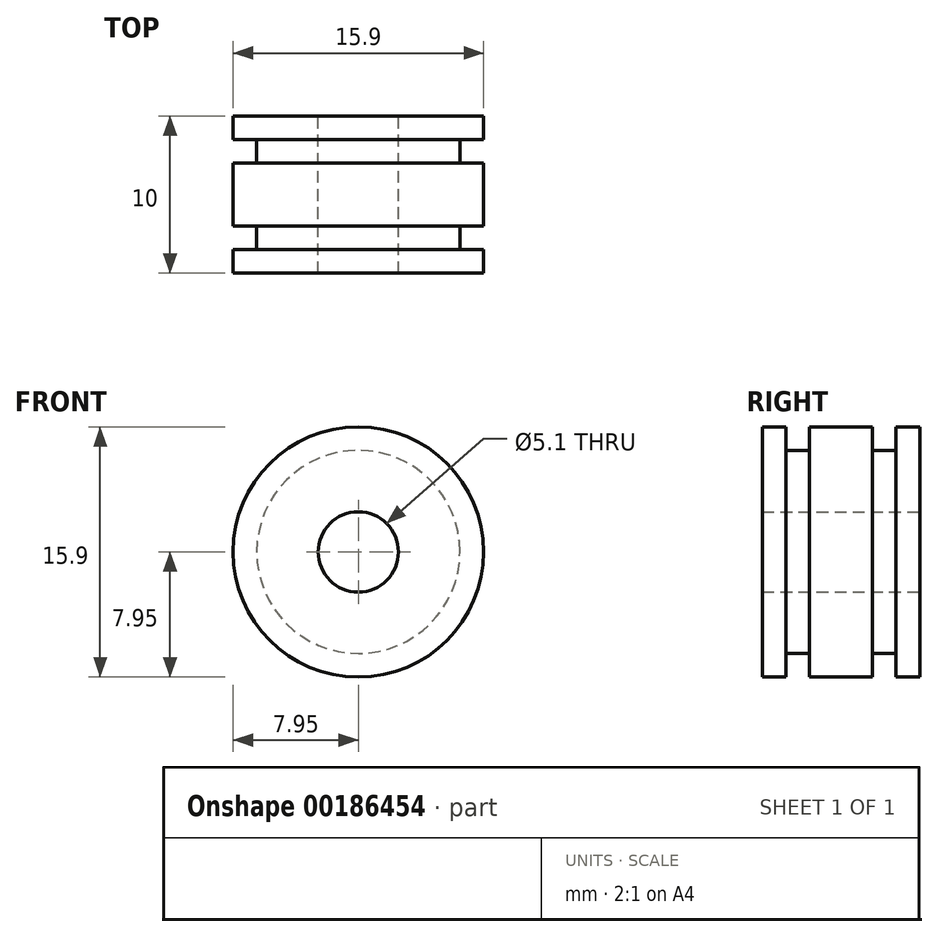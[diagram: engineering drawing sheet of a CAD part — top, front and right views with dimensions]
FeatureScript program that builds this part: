
annotation { "Feature Type Name" : "Feature", "Feature Type Description" : "" }
export const myFeature = defineFeature(function(context is Context, id is Id, definition is map)
    precondition{}
    {
        {
            var Q0;
            Q0=qCreatedBy(makeId("Right.planeOp"),FACE);
            var sketch = newSketch(context, id + "F0", { "sketchPlane" : qUnion([Q0])});
            skLineSegment(sketch, "E0", {"start": v(11.47, 0) * mm, "end": v(0, 0) * mm, "construction": true});
            skLineSegment(sketch, "E1", {"start": v(10, 2.55) * mm, "end": v(0, 2.55) * mm});
            skLineSegment(sketch, "E2", {"start": v(10, 2.55) * mm, "end": v(10, 4.42) * mm});
            skLineSegment(sketch, "E3", {"start": v(10, 4.42) * mm, "end": v(10, 4.42) * mm});
            skLineSegment(sketch, "E4", {"start": v(10, 4.42) * mm, "end": v(10, 7.95) * mm});
            skLineSegment(sketch, "E5", {"start": v(8.5, 7.95) * mm, "end": v(10, 7.95) * mm});
            skLineSegment(sketch, "E6", {"start": v(8.5, 7.95) * mm, "end": v(8.5, 6.45) * mm});
            skLineSegment(sketch, "E7", {"start": v(7, 6.45) * mm, "end": v(8.5, 6.45) * mm});
            skLineSegment(sketch, "E8", {"start": v(1.5, 6.45) * mm, "end": v(1.5, 7.95) * mm});
            skLineSegment(sketch, "E9", {"start": v(0, 7.95) * mm, "end": v(1.5, 7.95) * mm});
            skLineSegment(sketch, "E10", {"start": v(0, 7.95) * mm, "end": v(0, 2.55) * mm});
            skLineSegment(sketch, "E11", {"start": v(3, 6.45) * mm, "end": v(3, 7.95) * mm});
            skLineSegment(sketch, "E12", {"start": v(3, 7.95) * mm, "end": v(7, 7.95) * mm});
            skLineSegment(sketch, "E13", {"start": v(7, 7.95) * mm, "end": v(7, 6.45) * mm});
            skLineSegment(sketch, "E14.trimOffspring", {"start": v(3, 6.45) * mm, "end": v(1.5, 6.45) * mm});
            skSolve(sketch);
        }
        {
            var Q0;
            Q0=makeQuery(id+"F0.imprint","IMPRINT",FACE,{"disambiguationData":[TD([[makeQuery(id+"F0.imprint","IMPRINT",EDGE,{"derivedFrom":sQuery(id+"F0.wireOp",EDGE,"E1")}),-1.0]])]});
            var Q1;
            Q1=sQuery(id+"F0.wireOp",EDGE,"E0");
            revolve(context, id + "F1", {"entities" : qUnion([Q0]), "axis" : qUnion([Q1]), "revolveType" : RevolveType.FULL});
        }
    });
